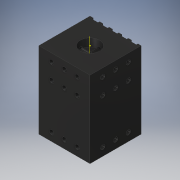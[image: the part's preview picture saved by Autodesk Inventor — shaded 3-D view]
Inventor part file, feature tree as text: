
AUTODESK INVENTOR PART (.ipt)
format: ipt  version: 2019 (Build 230136000, 136)  size: 359,936 bytes
history: native  units: mm
features: sketch x6, extrude x5, projected_geometry x3, other x1, pattern_circular x1, pattern_linear x1, reference x1
ambient origin geometry x8: Origin, YZ Plane, XZ Plane, XY Plane, X Axis, Y Axis, Z Axis, Center Point
bodies: Volumenkörper1 (feature_tree)
feature tree (18):
  extrude  "Extrusion1"  Depth=32.0mm
  extrude  "Extrusion2"  Depth=5.0mm
  extrude  "Extrusion3"  Depth=2.8mm
  extrude  "Extrusion4"  Depth=8.0mm
  other  "Arbeitsachse1"
  pattern_circular  "Runde Anordnung1"  [2 undecoded]
  sketch  "Sketch6"  dims[d12=2.8mm]
  extrude  "Extrusion6"  Depth=8.0mm TaperAngle=0.0deg
  pattern_linear  "Rectangular Pattern1"  Spacing1=12.0mm  [1 undecoded]
  sketch  "Skizze1"  dims[d0=32.0mm d1=32.0mm]
  sketch  "Skizze2"  dims[d2=48.0mm d3=0.0mm d4=5.0mm]
  projected_geometry  "Projizierte Kontur1"
  sketch  "Skizze3"  dims[d5=2.8mm d8=2.8mm]
  sketch  "Skizze4"  dims[d10=8.0mm d11=2.8mm]
  reference  "Referenz1"
  projected_geometry  "Projizierte Kontur2"
  sketch  "Sketch7"  dims[d13=8.0mm d14=0.0mm d15=5.0mm d16=8.0mm d17=0.0mm d18=12.0mm d19=5.0mm d20=0.0mm d23=10.0mm d28=40.0mm d29=360.0deg d40=8.0mm d41=8.0mm d42=8.0mm d43=8.0mm d44=2.8mm d45=2.8mm d46=2.8mm d47=2.8mm d48=2.0mm d49=2.0mm d50=1.0mm d51=0.0mm d52=30.0mm d54=6.0mm d55=30.0mm d57=6.0mm]
  projected_geometry  "Projected Loop3"
note: 3 required parameter values undecoded (feature->parameter linkage not recoverable at this tier; creation-order binding heuristic only, values carry confidence <= 0.55)
